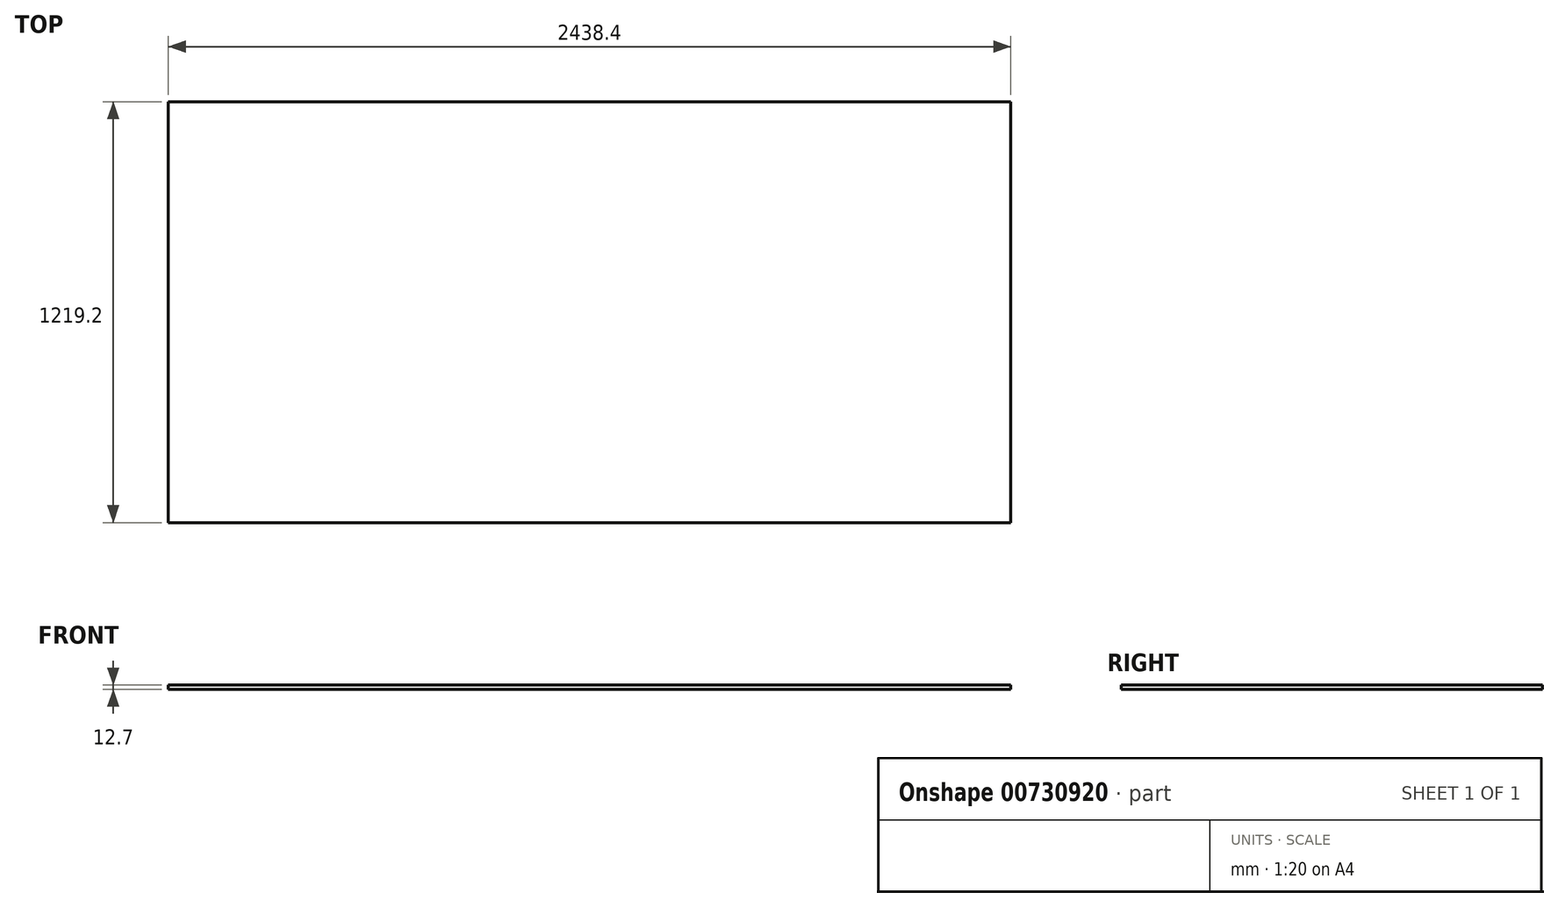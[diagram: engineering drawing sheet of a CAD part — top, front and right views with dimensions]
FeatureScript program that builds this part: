
annotation { "Feature Type Name" : "Feature", "Feature Type Description" : "" }
export const myFeature = defineFeature(function(context is Context, id is Id, definition is map)
    precondition{}
    {
        {
            var Q0;
            Q0=qCreatedBy(makeId("Top.planeOp"),FACE);
            var sketch = newSketch(context, id + "F0", { "sketchPlane" : qUnion([Q0])});
            skLineSegment(sketch, "E0.bottom", {"start": v(1219.2, 609.6) * mm, "end": v(-1219.2, 609.6) * mm});
            skLineSegment(sketch, "E0.top", {"start": v(1219.2, -609.6) * mm, "end": v(-1219.2, -609.6) * mm});
            skLineSegment(sketch, "E0.left", {"start": v(1219.2, 609.6) * mm, "end": v(1219.2, -609.6) * mm});
            skLineSegment(sketch, "E0.right", {"start": v(-1219.2, 609.6) * mm, "end": v(-1219.2, -609.6) * mm});
            skPoint(sketch, "E0.middle", {"position": v(0, 0) * mm});
            skSolve(sketch);
        }
        {
            var Q0;
            Q0=makeQuery(id+"F0.imprint","IMPRINT",FACE,{"disambiguationData":[TD([[makeQuery(id+"F0.imprint","IMPRINT",EDGE,{"derivedFrom":sQuery(id+"F0.wireOp",EDGE,"E0.bottom")}),1.0]])]});
            extrude(context, id + "F1", {"entities" : qUnion([Q0]), "depth" : 12.7 * mm, "offsetDistance" : 25.4 * mm});
        }
    });
